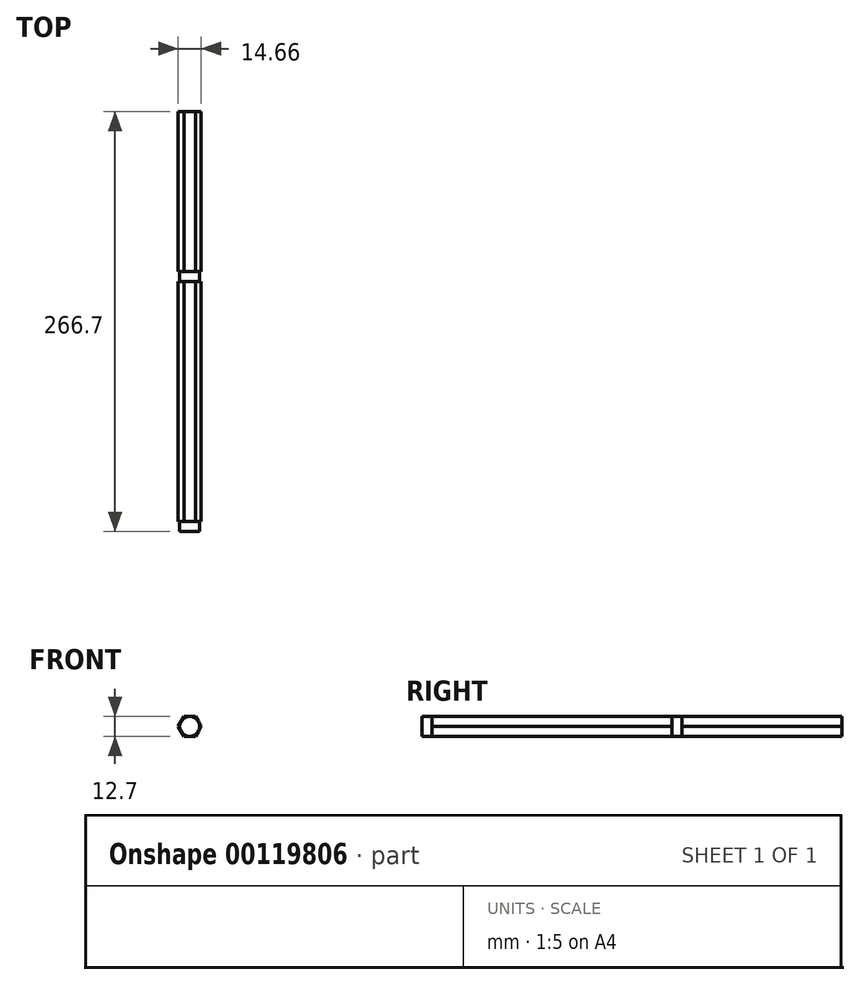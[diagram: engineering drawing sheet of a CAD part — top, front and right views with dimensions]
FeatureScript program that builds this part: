
annotation { "Feature Type Name" : "Feature", "Feature Type Description" : "" }
export const myFeature = defineFeature(function(context is Context, id is Id, definition is map)
    precondition{}
    {
        {
            var Q0;
            Q0=qCreatedBy(makeId("Front.planeOp"),FACE);
            var sketch = newSketch(context, id + "F0", { "sketchPlane" : qUnion([Q0])});
            skCircle(sketch, "E0.cCircle", {"center": v(0, 0) * mm, "radius": 6.35 * mm, "construction": true});
            skLineSegment(sketch, "E0.0", {"start": v(3.67, -6.35) * mm, "end": v(-3.67, -6.35) * mm});
            skLineSegment(sketch, "E0.1", {"start": v(-3.67, -6.35) * mm, "end": v(-7.33, 0) * mm});
            skLineSegment(sketch, "E0.2", {"start": v(-7.33, 0) * mm, "end": v(-3.67, 6.35) * mm});
            skLineSegment(sketch, "E0.3", {"start": v(-3.67, 6.35) * mm, "end": v(3.67, 6.35) * mm});
            skLineSegment(sketch, "E0.4", {"start": v(3.67, 6.35) * mm, "end": v(7.33, 0) * mm});
            skLineSegment(sketch, "E0.5", {"start": v(7.33, 0) * mm, "end": v(3.67, -6.35) * mm});
            skPoint(sketch, "E0.0.midPoint", {"position": v(0, -6.35) * mm});
            skSolve(sketch);
        }
        {
            var Q0;
            Q0 = qSketchRegion(id + "F0", true);
            extrude(context, id + "F1", {"entities" : qUnion([Q0]), "depth" : 152.4 * mm});
        }
        {
            var Q0;
            Q0=makeQuery(id+"F1.opExtrude","CAP_FACE",FACE,{"disambiguationData":[OSD([sQuery(id+"F0.wireOp",EDGE,"E0.0"),sQuery(id+"F0.wireOp",EDGE,"E0.1"),sQuery(id+"F0.wireOp",EDGE,"E0.2"),sQuery(id+"F0.wireOp",EDGE,"E0.3"),sQuery(id+"F0.wireOp",EDGE,"E0.4"),sQuery(id+"F0.wireOp",EDGE,"E0.5")])],"isStart":false});
            var sketch = newSketch(context, id + "F2", { "sketchPlane" : qUnion([Q0])});
            skCircle(sketch, "E1", {"center": v(0, 0) * mm, "radius": 6.35 * mm});
            skSolve(sketch);
        }
        {
            var Q0;
            {var subQ0=sQuery(id+"F2.wireOp",EDGE,"E1");var subQ4=makeQuery(id+"F2.imprint","INTERSECT",VERTEX,{"derivedFrom":[makeQuery(id+"F1.opExtrude","CAP_EDGE",EDGE,{"disambiguationData":[OSD([sQuery(id+"F0.wireOp",EDGE,"E0.3")])],"isStart":false}),subQ0]});Q0=makeQuery(id+"F2.imprint","IMPRINT",FACE,{"disambiguationData":[TD([[makeQuery(id+"F2.imprint","IMPRINT",EDGE,{"disambiguationData":[TD([[subQ4,1.0]])],"derivedFrom":subQ0}),1.0]])]});}
            extrude(context, id + "F3", {"entities" : qUnion([Q0]), "operationType" : NewBodyOperationType.ADD, "depth" : 6.35 * mm});
        }
        {
            var Q0;
            Q0=makeQuery(id+"F1.opExtrude","CAP_FACE",FACE,{"disambiguationData":[OSD([sQuery(id+"F0.wireOp",EDGE,"E0.0"),sQuery(id+"F0.wireOp",EDGE,"E0.1"),sQuery(id+"F0.wireOp",EDGE,"E0.2"),sQuery(id+"F0.wireOp",EDGE,"E0.3"),sQuery(id+"F0.wireOp",EDGE,"E0.4"),sQuery(id+"F0.wireOp",EDGE,"E0.5")])],"isStart":true});
            var sketch = newSketch(context, id + "F4", { "sketchPlane" : qUnion([Q0])});
            skCircle(sketch, "E2", {"center": v(0, 0) * mm, "radius": 6.35 * mm});
            skSolve(sketch);
        }
        {
            var Q0;
            {var subQ0=sQuery(id+"F4.wireOp",EDGE,"E2");var subQ3=makeQuery(id+"F4.imprint","INTERSECT",VERTEX,{"derivedFrom":[makeQuery(id+"F1.opExtrude","CAP_EDGE",EDGE,{"disambiguationData":[OSD([sQuery(id+"F0.wireOp",EDGE,"E0.3")])],"isStart":true}),subQ0]});Q0=makeQuery(id+"F4.imprint","IMPRINT",FACE,{"disambiguationData":[TD([[makeQuery(id+"F4.imprint","IMPRINT",EDGE,{"disambiguationData":[TD([[subQ3,1.0]])],"derivedFrom":subQ0}),1.0]])]});}
            extrude(context, id + "F5", {"entities" : qUnion([Q0]), "operationType" : NewBodyOperationType.ADD, "depth" : 6.35 * mm});
        }
        {
            var Q0;
            Q0=makeQuery(id+"F5.opExtrude","CAP_FACE",FACE,{"disambiguationData":[OSD([sQuery(id+"F4.wireOp",EDGE,"E2")])],"isStart":false});
            var sketch = newSketch(context, id + "F6", { "sketchPlane" : qUnion([Q0])});
            skCircle(sketch, "E3.cCircle", {"center": v(0, 0) * mm, "radius": 6.35 * mm, "construction": true});
            skLineSegment(sketch, "E3.0", {"start": v(3.67, -6.35) * mm, "end": v(-3.67, -6.35) * mm});
            skLineSegment(sketch, "E3.1", {"start": v(-3.67, -6.35) * mm, "end": v(-7.33, 0) * mm});
            skLineSegment(sketch, "E3.2", {"start": v(-7.33, 0) * mm, "end": v(-3.67, 6.35) * mm});
            skLineSegment(sketch, "E3.3", {"start": v(-3.67, 6.35) * mm, "end": v(3.67, 6.35) * mm});
            skLineSegment(sketch, "E3.4", {"start": v(3.67, 6.35) * mm, "end": v(7.33, 0) * mm});
            skLineSegment(sketch, "E3.5", {"start": v(7.33, 0) * mm, "end": v(3.67, -6.35) * mm});
            skPoint(sketch, "E3.0.midPoint", {"position": v(0, -6.35) * mm});
            skSolve(sketch);
        }
        {
            var Q0;
            {var subQ0=makeQuery(id+"F5.opExtrude","CAP_EDGE",EDGE,{"disambiguationData":[OSD([sQuery(id+"F4.wireOp",EDGE,"E2")])],"isStart":false});var subQ4=makeQuery(id+"F6.imprint","INTERSECT",VERTEX,{"derivedFrom":[subQ0,sQuery(id+"F6.wireOp",EDGE,"E3.0")]});Q0=makeQuery(id+"F6.imprint","IMPRINT",FACE,{"disambiguationData":[TD([[makeQuery(id+"F6.imprint","IMPRINT",EDGE,{"disambiguationData":[TD([[subQ4,1.0]])],"derivedFrom":subQ0}),1.0]])]});}
            var Q1;
            {var subQ0=sQuery(id+"F6.wireOp",EDGE,"E3.5");var subQ1=sQuery(id+"F6.wireOp",EDGE,"E3.0");var subQ2=makeQuery(id+"F6.imprint","INTERSECT",VERTEX,{"derivedFrom":[subQ1,subQ0]});Q1=makeQuery(id+"F6.imprint","IMPRINT",FACE,{"disambiguationData":[TD([[makeQuery(id+"F6.imprint","IMPRINT",EDGE,{"disambiguationData":[TD([[subQ2,-1.0]])],"derivedFrom":subQ1}),-1.0]])]});}
            var Q2;
            {var subQ0=sQuery(id+"F6.wireOp",EDGE,"E3.5");var subQ1=sQuery(id+"F6.wireOp",EDGE,"E3.4");var subQ2=makeQuery(id+"F6.imprint","INTERSECT",VERTEX,{"derivedFrom":[subQ1,subQ0]});Q2=makeQuery(id+"F6.imprint","IMPRINT",FACE,{"disambiguationData":[TD([[makeQuery(id+"F6.imprint","IMPRINT",EDGE,{"disambiguationData":[TD([[subQ2,1.0]])],"derivedFrom":subQ1}),-1.0]])]});}
            var Q3;
            {var subQ0=sQuery(id+"F6.wireOp",EDGE,"E3.4");var subQ1=sQuery(id+"F6.wireOp",EDGE,"E3.3");var subQ2=makeQuery(id+"F6.imprint","INTERSECT",VERTEX,{"derivedFrom":[subQ1,subQ0]});Q3=makeQuery(id+"F6.imprint","IMPRINT",FACE,{"disambiguationData":[TD([[makeQuery(id+"F6.imprint","IMPRINT",EDGE,{"disambiguationData":[TD([[subQ2,1.0]])],"derivedFrom":subQ1}),-1.0]])]});}
            var Q4;
            {var subQ0=sQuery(id+"F6.wireOp",EDGE,"E3.3");var subQ1=sQuery(id+"F6.wireOp",EDGE,"E3.2");var subQ2=makeQuery(id+"F6.imprint","INTERSECT",VERTEX,{"derivedFrom":[subQ1,subQ0]});Q4=makeQuery(id+"F6.imprint","IMPRINT",FACE,{"disambiguationData":[TD([[makeQuery(id+"F6.imprint","IMPRINT",EDGE,{"disambiguationData":[TD([[subQ2,1.0]])],"derivedFrom":subQ1}),-1.0]])]});}
            var Q5;
            {var subQ0=sQuery(id+"F6.wireOp",EDGE,"E3.2");var subQ1=sQuery(id+"F6.wireOp",EDGE,"E3.1");var subQ2=makeQuery(id+"F6.imprint","INTERSECT",VERTEX,{"derivedFrom":[subQ1,subQ0]});Q5=makeQuery(id+"F6.imprint","IMPRINT",FACE,{"disambiguationData":[TD([[makeQuery(id+"F6.imprint","IMPRINT",EDGE,{"disambiguationData":[TD([[subQ2,1.0]])],"derivedFrom":subQ1}),-1.0]])]});}
            var Q6;
            {var subQ0=sQuery(id+"F6.wireOp",EDGE,"E3.1");var subQ1=sQuery(id+"F6.wireOp",EDGE,"E3.0");var subQ2=makeQuery(id+"F6.imprint","INTERSECT",VERTEX,{"derivedFrom":[subQ1,subQ0]});Q6=makeQuery(id+"F6.imprint","IMPRINT",FACE,{"disambiguationData":[TD([[makeQuery(id+"F6.imprint","IMPRINT",EDGE,{"disambiguationData":[TD([[subQ2,1.0]])],"derivedFrom":subQ1}),-1.0]])]});}
            extrude(context, id + "F7", {"entities" : qUnion([Q0, Q1, Q2, Q3, Q4, Q5, Q6]), "operationType" : NewBodyOperationType.ADD, "depth" : 101.6 * mm});
        }
    });
